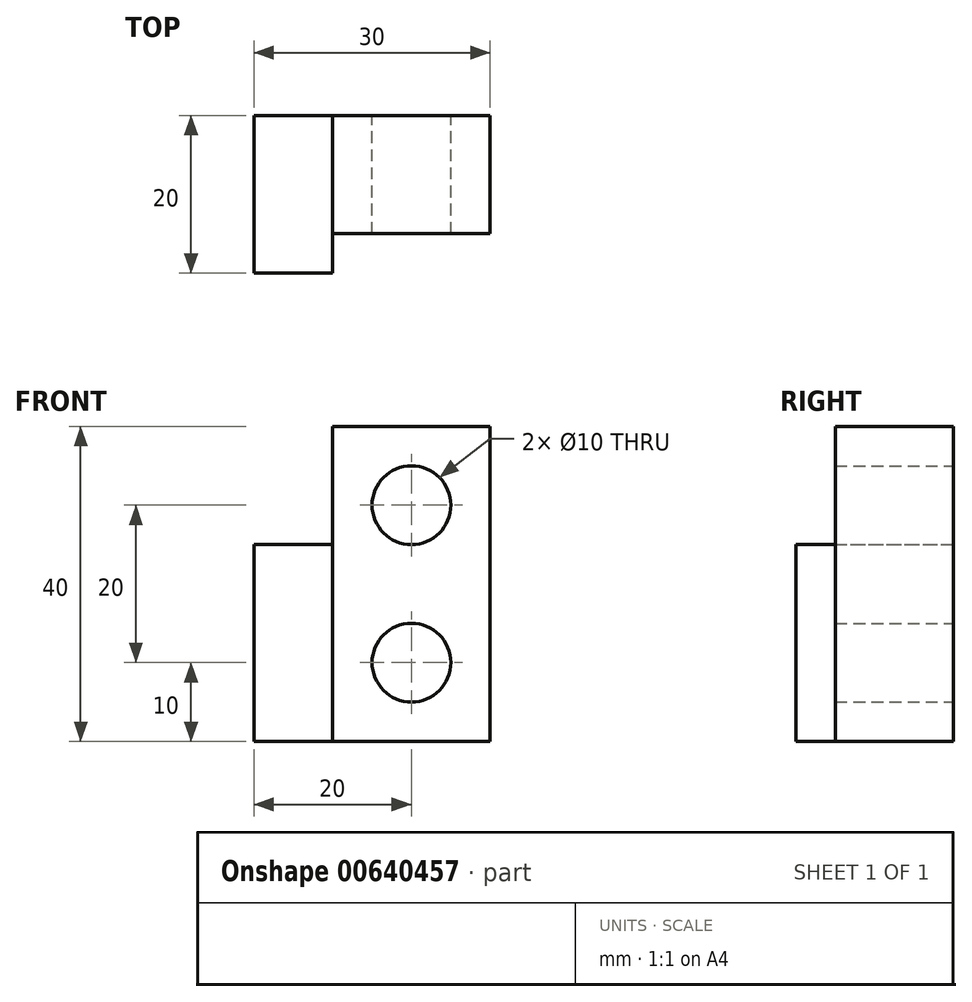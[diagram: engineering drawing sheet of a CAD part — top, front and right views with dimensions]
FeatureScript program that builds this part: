
annotation { "Feature Type Name" : "Feature", "Feature Type Description" : "" }
export const myFeature = defineFeature(function(context is Context, id is Id, definition is map)
    precondition{}
    {
        {
            var Q0;
            Q0=qCreatedBy(makeId("Front.planeOp"),FACE);
            var sketch = newSketch(context, id + "F0", { "sketchPlane" : qUnion([Q0])});
            skLineSegment(sketch, "E0.bottom", {"start": v(-10, 20) * mm, "end": v(10, 20) * mm});
            skLineSegment(sketch, "E0.top", {"start": v(-10, -20) * mm, "end": v(10, -20) * mm});
            skLineSegment(sketch, "E0.left", {"start": v(-10, 20) * mm, "end": v(-10, -20) * mm});
            skLineSegment(sketch, "E0.right", {"start": v(10, 20) * mm, "end": v(10, -20) * mm});
            skPoint(sketch, "E0.middle", {"position": v(0, 0) * mm});
            skLineSegment(sketch, "E1.bottom", {"start": v(-10, -20) * mm, "end": v(-20, -20) * mm});
            skLineSegment(sketch, "E1.top", {"start": v(-10, 5) * mm, "end": v(-20, 5) * mm});
            skLineSegment(sketch, "E1.left", {"start": v(-10, -20) * mm, "end": v(-10, 5) * mm});
            skLineSegment(sketch, "E1.right", {"start": v(-20, -20) * mm, "end": v(-20, 5) * mm});
            skCircle(sketch, "E2", {"center": v(0, -10) * mm, "radius": 5 * mm});
            skSolve(sketch);
        }
        {
            var Q0;
            Q0=makeQuery(id+"F0.imprint","IMPRINT",FACE,{"disambiguationData":[TD([[makeQuery(id+"F0.imprint","IMPRINT",EDGE,{"derivedFrom":sQuery(id+"F0.wireOp",EDGE,"E0.bottom")}),-1.0]])]});
            extrude(context, id + "F1", {"entities" : qUnion([Q0]), "depth" : 15 * mm, "offsetDistance" : 25 * mm});
        }
        {
            var Q0;
            Q0=makeQuery(id+"F0.imprint","IMPRINT",FACE,{"disambiguationData":[TD([[makeQuery(id+"F0.imprint","IMPRINT",EDGE,{"derivedFrom":sQuery(id+"F0.wireOp",EDGE,"E1.bottom")}),-1.0]])]});
            extrude(context, id + "F2", {"entities" : qUnion([Q0]), "operationType" : NewBodyOperationType.ADD, "depth" : 20 * mm, "offsetDistance" : 25 * mm});
        }
        {
            var Q0;
            Q0=qCreatedBy(makeId("Front.planeOp"),FACE);
            var sketch = newSketch(context, id + "F3", { "sketchPlane" : qUnion([Q0])});
            skCircle(sketch, "E3", {"center": v(0, 10) * mm, "radius": 5 * mm});
            skSolve(sketch);
        }
        {
            var Q0;
            Q0 = qSketchRegion(id + "F3", true);
            extrude(context, id + "F4", {"entities" : qUnion([Q0]), "operationType" : NewBodyOperationType.REMOVE, "oppositeDirection" : true, "depth" : 25 * mm, "offsetDistance" : 25 * mm});
        }
        {
            var Q0;
            Q0=sQuery(id+"F3.wireOp",VERTEX,"E3.center");
            var Q1;
            Q1=makeQuery(id+"F1.opExtrude","SWEPT_BODY",BODY,{"disambiguationData":[OSD([sQuery(id+"F0.wireOp",EDGE,"E0.bottom"),sQuery(id+"F0.wireOp",EDGE,"E0.top"),sQuery(id+"F0.wireOp",EDGE,"E0.left"),sQuery(id+"F0.wireOp",EDGE,"E0.right"),sQuery(id+"F0.wireOp",EDGE,"E1.left"),sQuery(id+"F0.wireOp",EDGE,"E2")])]});
            hole(context, id + "F5", {"style" : HoleStyle.SIMPLE, "endStyle" : HoleEndStyle.THROUGH, "oppositeDirection" : true, "holeDiameter" : 10 * mm, "majorDiameter" : 5 * mm, "isTappedThrough" : true, "tappedDepth" : 12 * mm, "tapClearance" : 3, "locations" : qUnion([Q0]), "scope" : qUnion([Q1])});
        }
    });
